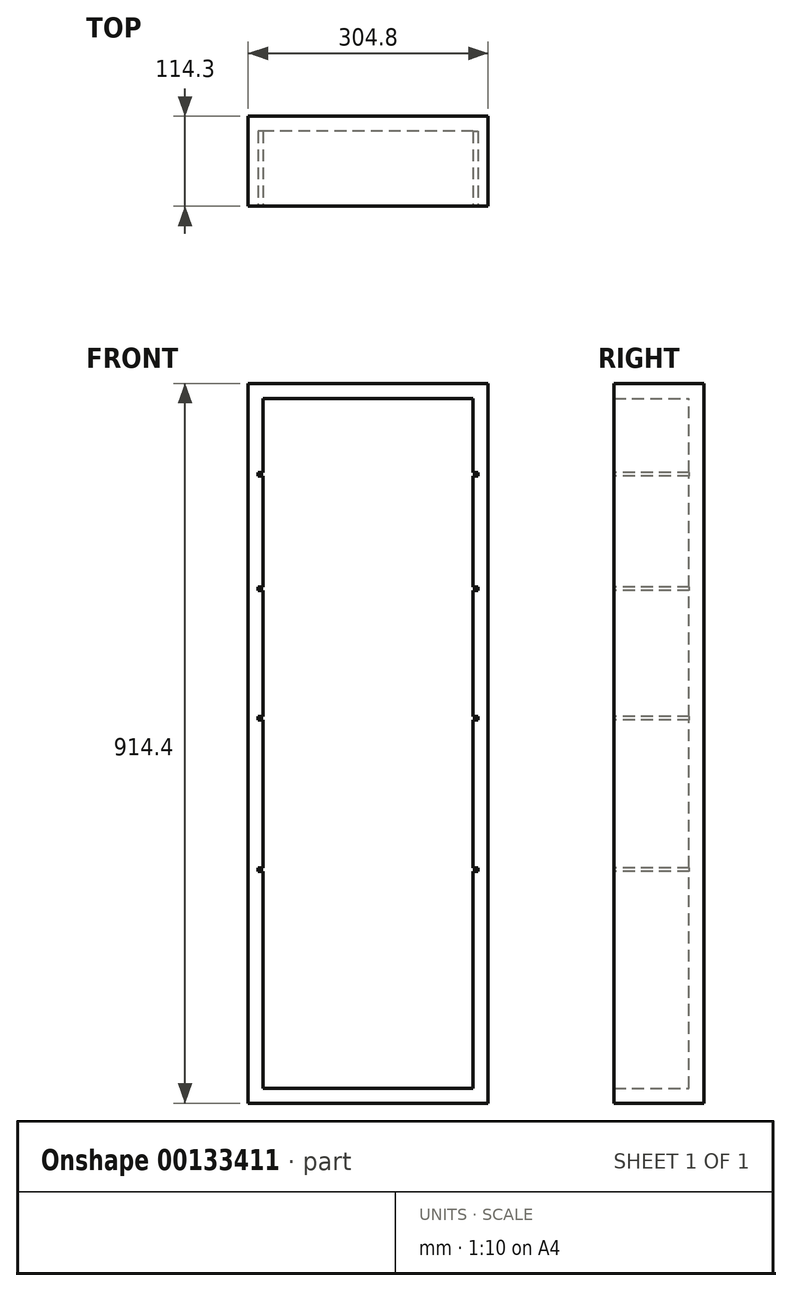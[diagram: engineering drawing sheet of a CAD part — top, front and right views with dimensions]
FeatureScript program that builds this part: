
annotation { "Feature Type Name" : "Feature", "Feature Type Description" : "" }
export const myFeature = defineFeature(function(context is Context, id is Id, definition is map)
    precondition{}
    {
        {
            var Q0;
            Q0=qCreatedBy(makeId("Front.planeOp"),FACE);
            var sketch = newSketch(context, id + "F0", { "sketchPlane" : qUnion([Q0])});
            skLineSegment(sketch, "E0.bottom", {"start": v(-152.4, 457.2) * mm, "end": v(152.4, 457.2) * mm});
            skLineSegment(sketch, "E0.top", {"start": v(-152.4, -457.2) * mm, "end": v(152.4, -457.2) * mm});
            skLineSegment(sketch, "E0.left", {"start": v(-152.4, 457.2) * mm, "end": v(-152.4, -457.2) * mm});
            skLineSegment(sketch, "E0.right", {"start": v(152.4, 457.2) * mm, "end": v(152.4, -457.2) * mm});
            skPoint(sketch, "E0.middle", {"position": v(0, 0) * mm});
            skLineSegment(sketch, "E1.bottom", {"start": v(-133.35, 438.15) * mm, "end": v(133.35, 438.15) * mm});
            skLineSegment(sketch, "E1.top", {"start": v(-133.35, -438.15) * mm, "end": v(133.35, -438.15) * mm});
            skLineSegment(sketch, "E1.left", {"start": v(-133.35, 438.15) * mm, "end": v(-133.35, -438.15) * mm});
            skLineSegment(sketch, "E1.right", {"start": v(133.35, 438.15) * mm, "end": v(133.35, -438.15) * mm});
            skLineSegment(sketch, "E2", {"start": v(-133.35, 438.15) * mm, "end": v(-152.4, 438.15) * mm, "construction": true});
            skLineSegment(sketch, "E3", {"start": v(-133.35, 438.15) * mm, "end": v(-133.35, 457.2) * mm, "construction": true});
            skSolve(sketch);
        }
        {
            var Q0;
            Q0 = qSketchRegion(id + "F0", true);
            extrude(context, id + "F1", {"entities" : qUnion([Q0]), "depth" : 114.3 * mm});
        }
        {
            var Q0;
            Q0=makeQuery(id+"F1.opExtrude","CAP_FACE",FACE,{"disambiguationData":[OSD([sQuery(id+"F0.wireOp",EDGE,"E0.bottom"),sQuery(id+"F0.wireOp",EDGE,"E0.top"),sQuery(id+"F0.wireOp",EDGE,"E0.left"),sQuery(id+"F0.wireOp",EDGE,"E0.right"),sQuery(id+"F0.wireOp",EDGE,"E1.bottom"),sQuery(id+"F0.wireOp",EDGE,"E1.top"),sQuery(id+"F0.wireOp",EDGE,"E1.left"),sQuery(id+"F0.wireOp",EDGE,"E1.right")])],"isStart":true});
            var sketch = newSketch(context, id + "F2", { "sketchPlane" : qUnion([Q0])});
            skLineSegment(sketch, "E4.bottom", {"start": v(-152.4, 457.2) * mm, "end": v(152.4, 457.2) * mm});
            skLineSegment(sketch, "E4.top", {"start": v(-152.4, -457.2) * mm, "end": v(152.4, -457.2) * mm});
            skLineSegment(sketch, "E4.left", {"start": v(-152.4, 457.2) * mm, "end": v(-152.4, -457.2) * mm});
            skLineSegment(sketch, "E4.right", {"start": v(152.4, 457.2) * mm, "end": v(152.4, -457.2) * mm});
            skSolve(sketch);
        }
        {
            var Q0;
            Q0 = qSketchRegion(id + "F2", true);
            extrude(context, id + "F3", {"entities" : qUnion([Q0]), "operationType" : NewBodyOperationType.ADD, "oppositeDirection" : true, "depth" : 19.05 * mm});
        }
        {
            var Q0;
            Q0=makeQuery(id+"F1.opExtrude","CAP_FACE",FACE,{"disambiguationData":[OSD([sQuery(id+"F0.wireOp",EDGE,"E0.bottom"),sQuery(id+"F0.wireOp",EDGE,"E0.top"),sQuery(id+"F0.wireOp",EDGE,"E0.left"),sQuery(id+"F0.wireOp",EDGE,"E0.right"),sQuery(id+"F0.wireOp",EDGE,"E1.bottom"),sQuery(id+"F0.wireOp",EDGE,"E1.top"),sQuery(id+"F0.wireOp",EDGE,"E1.left"),sQuery(id+"F0.wireOp",EDGE,"E1.right")])],"isStart":false});
            var sketch = newSketch(context, id + "F4", { "sketchPlane" : qUnion([Q0])});
            skLineSegment(sketch, "E5", {"start": v(0, 438.15) * mm, "end": v(0, -438.15) * mm, "construction": true});
            skLineSegment(sketch, "E6.bottom", {"start": v(-133.35, 344.04) * mm, "end": v(-139.7, 344.04) * mm});
            skLineSegment(sketch, "E6.top", {"start": v(-133.35, 339.6) * mm, "end": v(-139.7, 339.6) * mm});
            skLineSegment(sketch, "E6.left", {"start": v(-133.35, 344.04) * mm, "end": v(-133.35, 339.6) * mm});
            skLineSegment(sketch, "E6.right", {"start": v(-139.7, 344.04) * mm, "end": v(-139.7, 339.6) * mm});
            skLineSegment(sketch, "E7.bottom", {"start": v(-133.35, 198.37) * mm, "end": v(-139.7, 198.37) * mm});
            skLineSegment(sketch, "E7.top", {"start": v(-133.35, 193.93) * mm, "end": v(-139.7, 193.93) * mm});
            skLineSegment(sketch, "E7.left", {"start": v(-133.35, 198.37) * mm, "end": v(-133.35, 193.93) * mm});
            skLineSegment(sketch, "E7.right", {"start": v(-139.7, 198.37) * mm, "end": v(-139.7, 193.93) * mm});
            skPoint(sketch, "E8.oppositeSnap0", {"position": v(-139.7, 196.15) * mm});
            skLineSegment(sketch, "E8.bottom", {"start": v(-133.35, 33.8) * mm, "end": v(-139.7, 33.8) * mm});
            skLineSegment(sketch, "E8.top", {"start": v(-133.35, 29.35) * mm, "end": v(-139.7, 29.35) * mm});
            skLineSegment(sketch, "E8.left", {"start": v(-133.35, 33.8) * mm, "end": v(-133.35, 29.35) * mm});
            skLineSegment(sketch, "E8.right", {"start": v(-139.7, 33.8) * mm, "end": v(-139.7, 29.35) * mm});
            skLineSegment(sketch, "E9.bottom", {"start": v(-133.35, -158.17) * mm, "end": v(-139.7, -158.17) * mm});
            skLineSegment(sketch, "E9.top", {"start": v(-133.35, -162.61) * mm, "end": v(-139.7, -162.61) * mm});
            skLineSegment(sketch, "E9.left", {"start": v(-133.35, -158.17) * mm, "end": v(-133.35, -162.61) * mm});
            skLineSegment(sketch, "E9.right", {"start": v(-139.7, -158.17) * mm, "end": v(-139.7, -162.61) * mm});
            skLineSegment(sketch, "E10.MirrorCS", {"start": v(133.35, 193.93) * mm, "end": v(139.7, 193.93) * mm});
            skLineSegment(sketch, "E11.MirrorCS", {"start": v(133.35, 339.6) * mm, "end": v(139.7, 339.6) * mm});
            skLineSegment(sketch, "E12.MirrorCS", {"start": v(139.7, -158.17) * mm, "end": v(139.7, -162.61) * mm});
            skLineSegment(sketch, "E13.MirrorCS", {"start": v(133.35, 198.37) * mm, "end": v(133.35, 193.93) * mm});
            skLineSegment(sketch, "E14.MirrorCS", {"start": v(133.35, 198.37) * mm, "end": v(139.7, 198.37) * mm});
            skLineSegment(sketch, "E15.MirrorCS", {"start": v(139.7, 344.04) * mm, "end": v(139.7, 339.6) * mm});
            skLineSegment(sketch, "E16.MirrorCS", {"start": v(133.35, 344.04) * mm, "end": v(133.35, 339.6) * mm});
            skLineSegment(sketch, "E17.MirrorCS", {"start": v(133.35, 344.04) * mm, "end": v(139.7, 344.04) * mm});
            skLineSegment(sketch, "E18.MirrorCS", {"start": v(133.35, 29.35) * mm, "end": v(139.7, 29.35) * mm});
            skLineSegment(sketch, "E19.MirrorCS", {"start": v(139.7, 198.37) * mm, "end": v(139.7, 193.93) * mm});
            skLineSegment(sketch, "E20.MirrorCS", {"start": v(139.7, 33.8) * mm, "end": v(139.7, 29.35) * mm});
            skLineSegment(sketch, "E21.MirrorCS", {"start": v(133.35, -158.17) * mm, "end": v(139.7, -158.17) * mm});
            skLineSegment(sketch, "E22.MirrorCS", {"start": v(133.35, -162.61) * mm, "end": v(139.7, -162.61) * mm});
            skLineSegment(sketch, "E23.MirrorCS", {"start": v(133.35, -158.17) * mm, "end": v(133.35, -162.61) * mm});
            skLineSegment(sketch, "E24.MirrorCS", {"start": v(133.35, 33.8) * mm, "end": v(139.7, 33.8) * mm});
            skLineSegment(sketch, "E25.MirrorCS", {"start": v(133.35, 33.8) * mm, "end": v(133.35, 29.35) * mm});
            skPoint(sketch, "E26.MirrorP", {"position": v(139.7, 196.15) * mm});
            skSolve(sketch);
        }
        {
            var Q0;
            Q0 = qSketchRegion(id + "F4", true);
            extrude(context, id + "F5", {"entities" : qUnion([Q0]), "operationType" : NewBodyOperationType.REMOVE, "oppositeDirection" : true, "depth" : 95.25 * mm});
        }
    });
